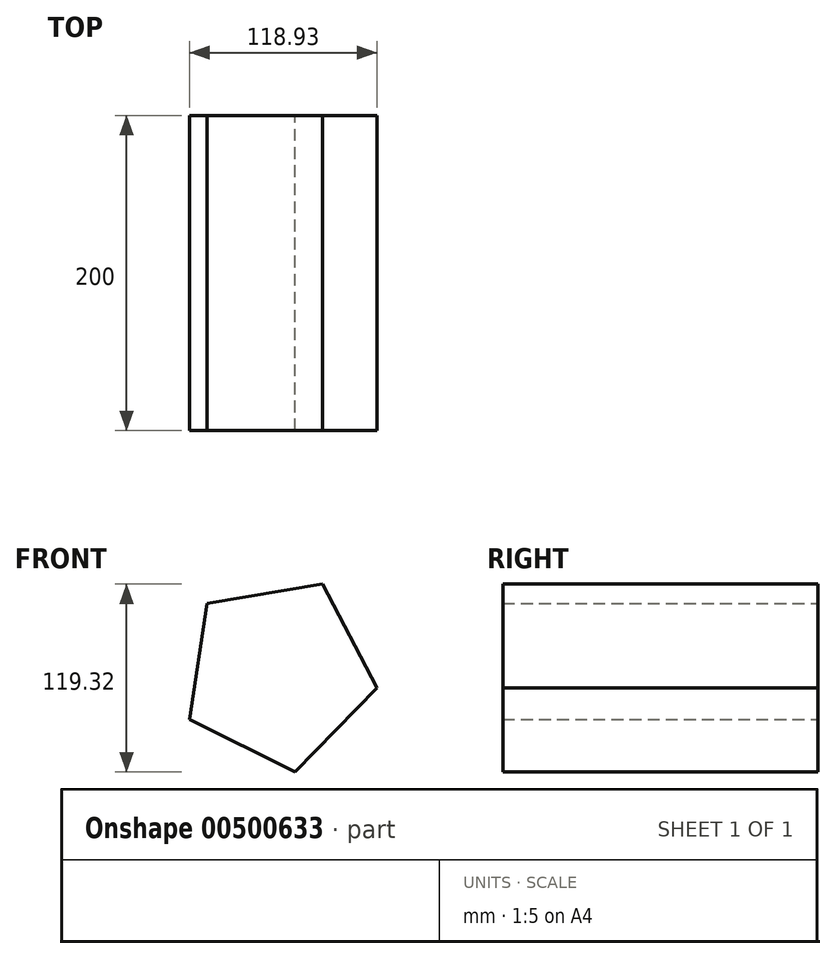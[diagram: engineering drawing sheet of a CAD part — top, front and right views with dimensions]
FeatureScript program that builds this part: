
annotation { "Feature Type Name" : "Feature", "Feature Type Description" : "" }
export const myFeature = defineFeature(function(context is Context, id is Id, definition is map)
    precondition{}
    {
        {
            var Q0;
            Q0=qCreatedBy(makeId("Front.planeOp"),FACE);
            var sketch = newSketch(context, id + "F0", { "sketchPlane" : qUnion([Q0])});
            skCircle(sketch, "E0.cCircle", {"center": v(0, 0) * mm, "radius": 51.3 * mm, "construction": true});
            skLineSegment(sketch, "E0.0", {"start": v(28.21, 56.8) * mm, "end": v(62.73, -9.28) * mm});
            skLineSegment(sketch, "E0.1", {"start": v(62.73, -9.28) * mm, "end": v(10.56, -62.53) * mm});
            skLineSegment(sketch, "E0.2", {"start": v(10.56, -62.53) * mm, "end": v(-56.2, -29.36) * mm});
            skLineSegment(sketch, "E0.3", {"start": v(-56.2, -29.36) * mm, "end": v(-45.3, 44.38) * mm});
            skLineSegment(sketch, "E0.4", {"start": v(-45.3, 44.38) * mm, "end": v(28.21, 56.8) * mm});
            skPoint(sketch, "E0.0.midPoint", {"position": v(45.47, 23.76) * mm});
            skSolve(sketch);
        }
        {
            var Q0;
            Q0=makeQuery(id+"F0.imprint","IMPRINT",FACE,{"disambiguationData":[TD([[makeQuery(id+"F0.imprint","IMPRINT",EDGE,{"derivedFrom":sQuery(id+"F0.wireOp",EDGE,"E0.0")}),-1.0]])]});
            extrude(context, id + "F1", {"entities" : qUnion([Q0]), "depth" : 200 * mm});
        }
    });
